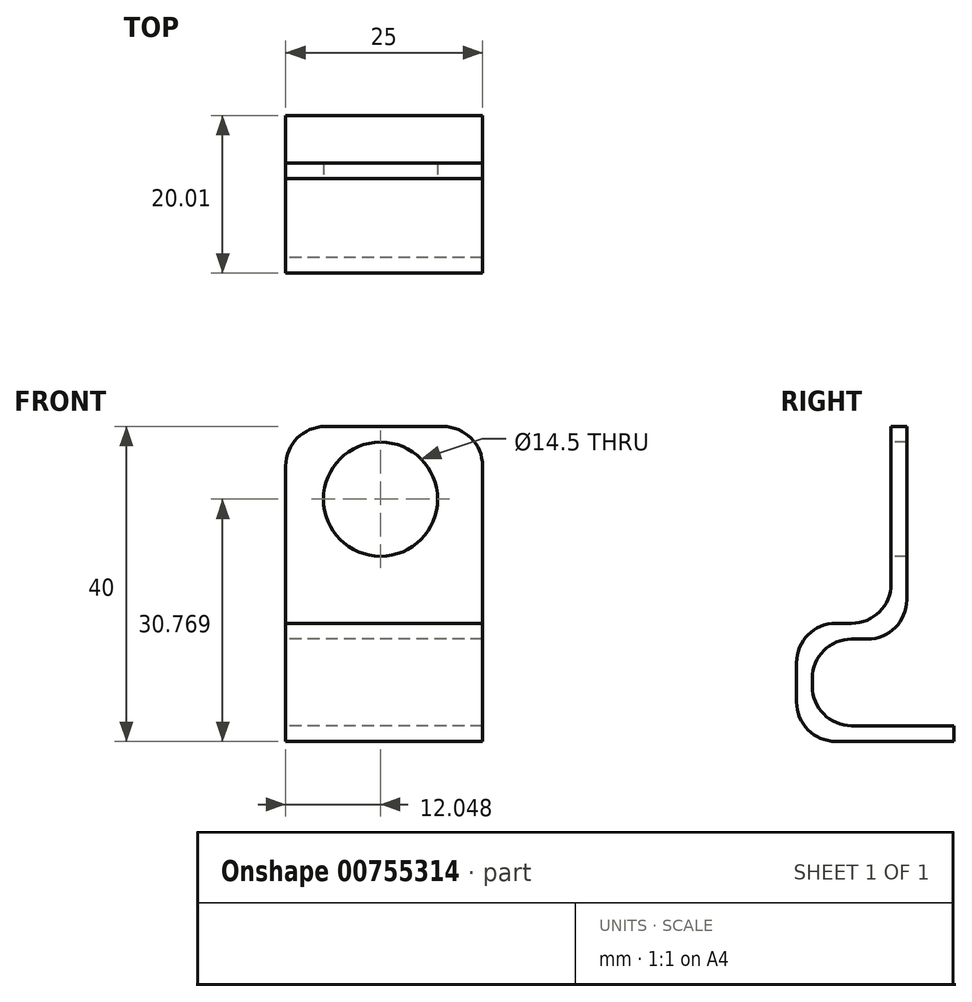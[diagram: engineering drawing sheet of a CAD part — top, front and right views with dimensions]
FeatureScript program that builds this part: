
annotation { "Feature Type Name" : "Feature", "Feature Type Description" : "" }
export const myFeature = defineFeature(function(context is Context, id is Id, definition is map)
    precondition{}
    {
        {
            var Q0;
            Q0=qCreatedBy(makeId("Right.planeOp"),FACE);
            var sketch = newSketch(context, id + "F0", { "sketchPlane" : qUnion([Q0])});
            skLineSegment(sketch, "E0", {"start": v(4.06, 29.32) * mm, "end": v(4.06, 4.32) * mm});
            skLineSegment(sketch, "E1", {"start": v(4.06, 4.32) * mm, "end": v(-7.94, 4.32) * mm});
            skLineSegment(sketch, "E2", {"start": v(-7.94, 4.32) * mm, "end": v(-7.94, -10.68) * mm});
            skLineSegment(sketch, "E3", {"start": v(-7.94, -10.68) * mm, "end": v(12.06, -10.68) * mm});
            skLineSegment(sketch, "E4", {"start": v(4.06, 29.32) * mm, "end": v(6.06, 29.32) * mm});
            skLineSegment(sketch, "E5", {"start": v(6.06, 29.32) * mm, "end": v(6.06, 2.32) * mm});
            skLineSegment(sketch, "E6", {"start": v(6.06, 2.32) * mm, "end": v(-5.94, 2.32) * mm});
            skLineSegment(sketch, "E7", {"start": v(-5.94, 2.32) * mm, "end": v(-5.94, -8.68) * mm});
            skLineSegment(sketch, "E8", {"start": v(-5.94, -8.68) * mm, "end": v(12.07, -8.68) * mm});
            skLineSegment(sketch, "E9", {"start": v(12.07, -8.68) * mm, "end": v(12.06, -10.68) * mm});
            skSolve(sketch);
        }
        {
            var Q0;
            Q0=makeQuery(id+"F0.imprint","IMPRINT",FACE,{"disambiguationData":[TD([[makeQuery(id+"F0.imprint","IMPRINT",EDGE,{"derivedFrom":sQuery(id+"F0.wireOp",EDGE,"E0")}),1.0]])]});
            extrude(context, id + "F1", {"entities" : qUnion([Q0]), "depth" : 25 * mm, "offsetDistance" : 25 * mm});
        }
        {
            var Q0;
            Q0=makeQuery(id+"F1.opExtrude","SWEPT_EDGE",EDGE,{"disambiguationData":[OSD([sQuery(id+"F0.wireOp",EDGE,"E0"),sQuery(id+"F0.wireOp",EDGE,"E1")])]});
            var Q1;
            Q1=makeQuery(id+"F1.opExtrude","SWEPT_EDGE",EDGE,{"disambiguationData":[OSD([sQuery(id+"F0.wireOp",EDGE,"E1"),sQuery(id+"F0.wireOp",EDGE,"E2")])]});
            var Q2;
            Q2=makeQuery(id+"F1.opExtrude","SWEPT_EDGE",EDGE,{"disambiguationData":[OSD([sQuery(id+"F0.wireOp",EDGE,"E2"),sQuery(id+"F0.wireOp",EDGE,"E3")])]});
            var Q3;
            Q3=makeQuery(id+"F1.opExtrude","SWEPT_EDGE",EDGE,{"disambiguationData":[OSD([sQuery(id+"F0.wireOp",EDGE,"E6"),sQuery(id+"F0.wireOp",EDGE,"E7")])]});
            var Q4;
            Q4=makeQuery(id+"F1.opExtrude","SWEPT_EDGE",EDGE,{"disambiguationData":[OSD([sQuery(id+"F0.wireOp",EDGE,"E7"),sQuery(id+"F0.wireOp",EDGE,"E8")])]});
            var Q5;
            Q5=makeQuery(id+"F1.opExtrude","SWEPT_EDGE",EDGE,{"disambiguationData":[OSD([sQuery(id+"F0.wireOp",EDGE,"E5"),sQuery(id+"F0.wireOp",EDGE,"E6")])]});
            var Q6;
            Q6=makeQuery(id+"F1.opExtrude","CAP_EDGE",EDGE,{"disambiguationData":[OSD([sQuery(id+"F0.wireOp",EDGE,"E4")])],"isStart":false});
            var Q7;
            Q7=makeQuery(id+"F1.opExtrude","CAP_EDGE",EDGE,{"disambiguationData":[OSD([sQuery(id+"F0.wireOp",EDGE,"E4")])],"isStart":true});
            fillet(context, id + "F2", {"entities" : qUnion([Q0, Q1, Q2, Q3, Q4, Q5, Q6, Q7]), "radius" : 5 * mm, "tangentPropagation" : true, "allowEdgeOverflow" : false});
        }
        {
            var Q0;
            Q0=qCreatedBy(makeId("Front.planeOp"),FACE);
            var sketch = newSketch(context, id + "F3", { "sketchPlane" : qUnion([Q0])});
            skCircle(sketch, "E10", {"center": v(12.05, 20.09) * mm, "radius": 7.25 * mm});
            skSolve(sketch);
        }
        {
            var Q0;
            Q0=makeQuery(id+"F3.imprint","IMPRINT",FACE,{"disambiguationData":[TD([[makeQuery(id+"F3.imprint","IMPRINT",EDGE,{"derivedFrom":sQuery(id+"F3.wireOp",EDGE,"E10")}),1.0]])]});
            extrude(context, id + "F4", {"entities" : qUnion([Q0]), "operationType" : NewBodyOperationType.REMOVE, "oppositeDirection" : true, "depth" : 25 * mm, "offsetDistance" : 25 * mm});
        }
    });
